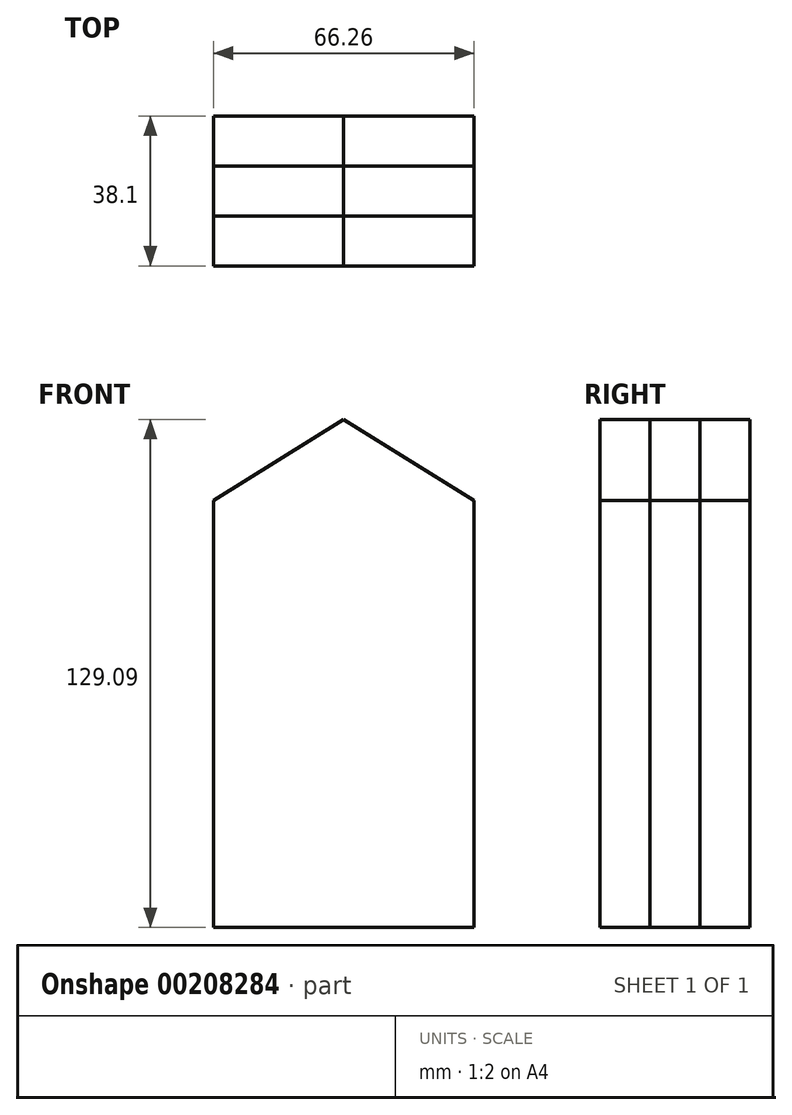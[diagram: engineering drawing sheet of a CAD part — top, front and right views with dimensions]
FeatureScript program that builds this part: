
annotation { "Feature Type Name" : "Feature", "Feature Type Description" : "" }
export const myFeature = defineFeature(function(context is Context, id is Id, definition is map)
    precondition{}
    {
        {
            var Q0;
            Q0=qCreatedBy(makeId("Front.planeOp"),FACE);
            var sketch = newSketch(context, id + "F0", { "sketchPlane" : qUnion([Q0])});
            skLineSegment(sketch, "E0.bottom", {"start": v(33.13, -54.23) * mm, "end": v(-33.13, -54.23) * mm});
            skLineSegment(sketch, "E0.top", {"start": v(33.13, 54.23) * mm, "end": v(-33.13, 54.23) * mm});
            skLineSegment(sketch, "E0.left", {"start": v(33.13, -54.23) * mm, "end": v(33.13, 54.23) * mm});
            skLineSegment(sketch, "E0.right", {"start": v(-33.13, -54.23) * mm, "end": v(-33.13, 54.23) * mm});
            skPoint(sketch, "E0.middle", {"position": v(0, 0) * mm});
            skLineSegment(sketch, "E1.bottom", {"start": v(0, 67.67) * mm, "end": v(0, 67.67) * mm});
            skLineSegment(sketch, "E1.top", {"start": v(0, 40.8) * mm, "end": v(0, 40.8) * mm});
            skLineSegment(sketch, "E1.left", {"start": v(0, 67.67) * mm, "end": v(0, 40.8) * mm});
            skLineSegment(sketch, "E1.right", {"start": v(0, 67.67) * mm, "end": v(0, 40.8) * mm});
            skPoint(sketch, "E1.middle", {"position": v(0, 54.23) * mm});
            skLineSegment(sketch, "E2", {"start": v(0, 74.86) * mm, "end": v(33.13, 54.23) * mm});
            skLineSegment(sketch, "E3.MirrorCS", {"start": v(0, 74.86) * mm, "end": v(-33.13, 54.23) * mm});
            skSolve(sketch);
        }
        {
            var Q0;
            {var subQ0=sQuery(id+"F0.wireOp",EDGE,"E2");Q0=makeQuery(id+"F0.imprint","IMPRINT",FACE,{"disambiguationData":[TD([[makeQuery(id+"F0.imprint","IMPRINT",EDGE,{"derivedFrom":subQ0}),-1.0]])]});}
            var Q1;
            Q1=makeQuery(id+"F0.imprint","IMPRINT",FACE,{"disambiguationData":[TD([[makeQuery(id+"F0.imprint","IMPRINT",EDGE,{"derivedFrom":sQuery(id+"F0.wireOp",EDGE,"E0.bottom")}),-1.0]])]});
            extrude(context, id + "F1", {"entities" : qUnion([Q0, Q1]), "oppositeDirection" : true, "depth" : 25.4 * mm});
        }
        {
            var Q0;
            Q0=makeQuery(id+"F1.opExtrude","CAP_FACE",FACE,{"disambiguationData":[OSD([sQuery(id+"F0.wireOp",EDGE,"E0.bottom"),sQuery(id+"F0.wireOp",EDGE,"E0.left"),sQuery(id+"F0.wireOp",EDGE,"E0.right"),sQuery(id+"F0.wireOp",EDGE,"E2"),sQuery(id+"F0.wireOp",EDGE,"E3.MirrorCS")])],"isStart":true});
            extrude(context, id + "F2", {"entities" : qUnion([Q0]), "endBound" : BoundingType.SYMMETRIC, "oppositeDirection" : true, "depth" : 25.4 * mm});
        }
    });
